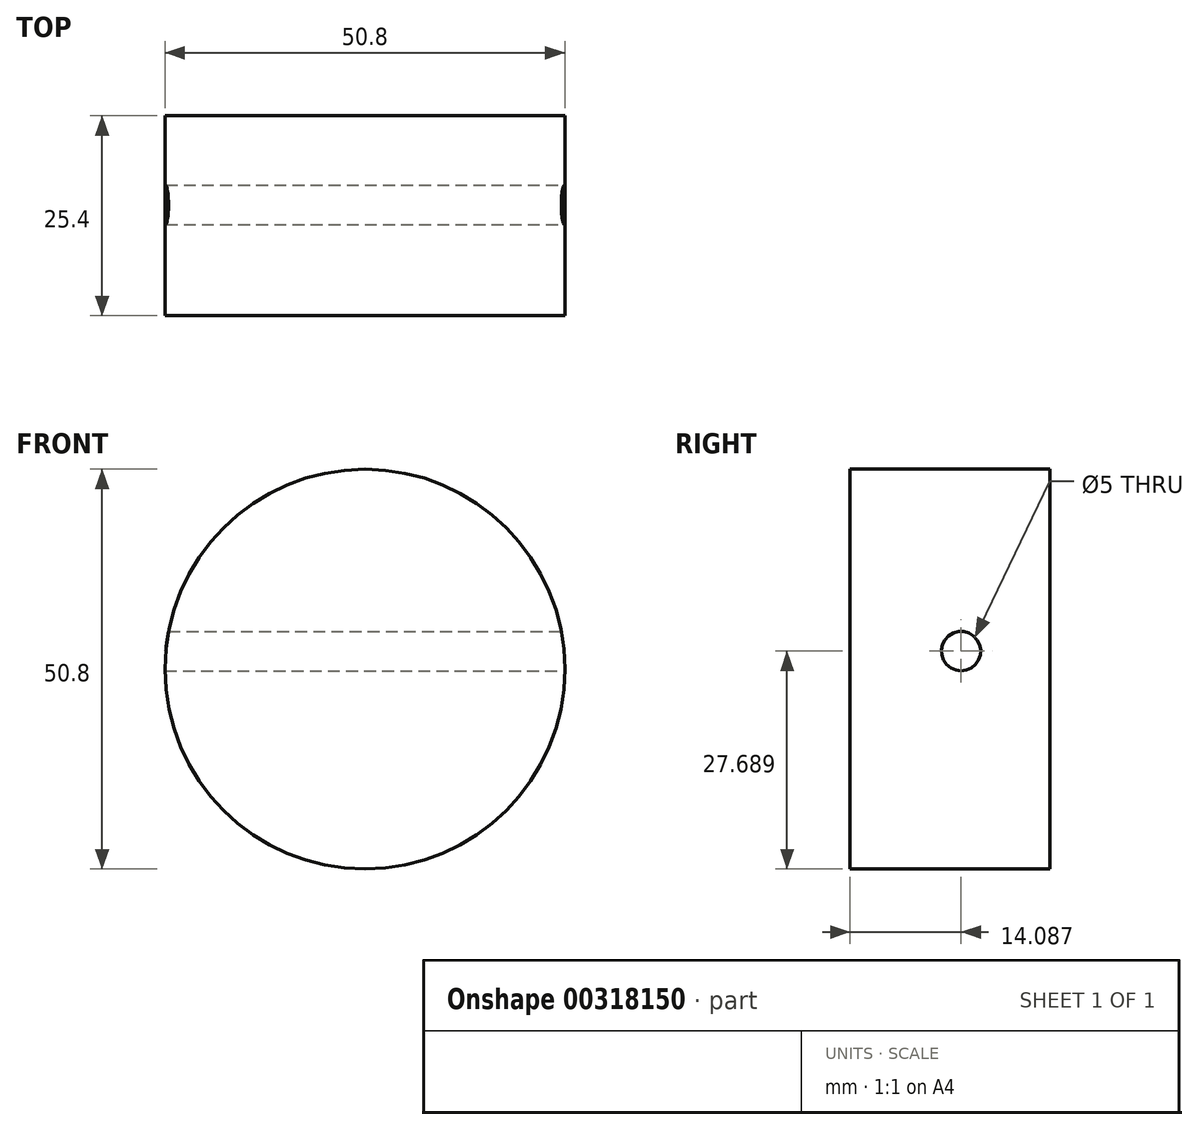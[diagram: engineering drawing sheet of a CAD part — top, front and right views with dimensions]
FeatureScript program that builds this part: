
annotation { "Feature Type Name" : "Feature", "Feature Type Description" : "" }
export const myFeature = defineFeature(function(context is Context, id is Id, definition is map)
    precondition{}
    {
        {
            var Q0;
            Q0=qCreatedBy(makeId("Front.planeOp"),FACE);
            var sketch = newSketch(context, id + "F0", { "sketchPlane" : qUnion([Q0])});
            skCircle(sketch, "E0", {"center": v(-44.67, 54.92) * mm, "radius": 25.4 * mm});
            skSolve(sketch);
        }
        {
            var Q0;
            Q0=makeQuery(id+"F0.imprint","IMPRINT",FACE,{"disambiguationData":[TD([[makeQuery(id+"F0.imprint","IMPRINT",EDGE,{"derivedFrom":sQuery(id+"F0.wireOp",EDGE,"E0")}),1.0]])]});
            extrude(context, id + "F1", {"entities" : qUnion([Q0]), "depth" : 25.4 * mm});
        }
        {
            var Q0;
            Q0=qCreatedBy(makeId("Right.planeOp"),FACE);
            var sketch = newSketch(context, id + "F2", { "sketchPlane" : qUnion([Q0])});
            skPoint(sketch, "E1", {"position": v(-11.31, 57.2) * mm});
            skPoint(sketch, "E2", {"position": v(-25.77, 57.2) * mm});
            skPoint(sketch, "E3", {"position": v(0, 57.2) * mm});
            skSolve(sketch);
        }
        {
            var Q0;
            Q0=sQuery(id+"F2.wireOp",VERTEX,"E1");
            var Q1;
            Q1=makeQuery(id+"F1.opExtrude","SWEPT_BODY",BODY,{"disambiguationData":[OSD([sQuery(id+"F0.wireOp",EDGE,"E0")])]});
            hole(context, id + "F3", {"style" : HoleStyle.C_SINK, "endStyle" : HoleEndStyle.THROUGH, "standardTappedOrClearance" : lookupTablePath({ "standard" : "ISO", "size" : "5", "type" : "Drilled" }), "standardBlindInLast" : lookupTablePath({ "standard" : "ISO", "size" : "5", "type" : "Drilled" }), "holeDiameter" : 5 * mm, "cSinkDiameter" : 11.2 * mm, "cSinkAngle" : 45 * degree, "tappedDepth" : 12.7 * mm, "tapClearance" : 3, "startFromSketch" : true, "locations" : qUnion([Q0]), "scope" : qUnion([Q1])});
        }
    });
